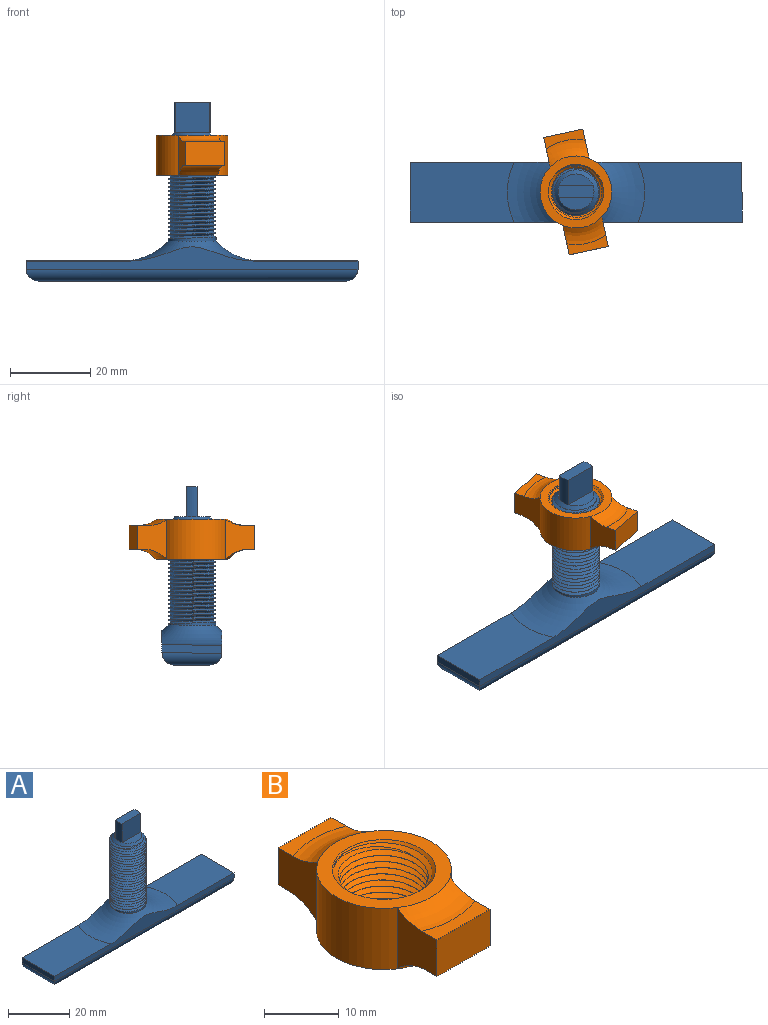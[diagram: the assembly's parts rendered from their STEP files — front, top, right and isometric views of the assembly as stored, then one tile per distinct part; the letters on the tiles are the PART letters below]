
ASSEMBLY  parts=2 mates=1
PART A: 24 faces, bbox 83x60.2x44.5 mm
  f0: plane 8.5x3.02mm, normal (0,0,1), area 18.7mm2, adj f15,f22
  f1: plane 26.04x15mm, normal (0,0,1), area 373.2mm2, adj f2,f4,f5,f12
  f2: plane 83x5.55mm, normal (0,-1,0), area 215.5mm2, adj f1,f3,f5,f6,f8,f12
  f3: plane 15x2mm, normal (1,0,0), area 30mm2, adj f2,f4,f6,f9
  f4: plane 83x5.55mm, normal (0,1,0), area 215.5mm2, adj f1,f3,f5,f6,f11,f12
  f5: plane 15x2mm, normal (-1,0,0), area 30mm2, adj f1,f2,f4,f10
  f6: plane 26.04x15mm, normal (0,0,1), area 373.2mm2, adj f2,f3,f4,f12
  f7: plane 77x9mm, normal (0,0,-1), area 693mm2, adj f8,f9,f10,f11
  f8: cylinder r=3mm len=83mm, axis (1,0,0), area 377mm2, adj f2,f7,f9,f10
  f9: cylinder r=3mm len=15mm, axis (0,1,0), area 56.5mm2, adj f3,f7,f8,f11
  f10: cylinder r=3mm len=15mm, axis (0,-1,0), area 56.5mm2, adj f5,f7,f8,f11
  f11: cylinder r=3mm len=83mm, axis (-1,0,0), area 377mm2, adj f4,f7,f9,f10
  f12: torus R=17.18mm, axis (0,0,1), area 440.4mm2, adj f1,f2,f4,f6,f13
  f13: cylinder r=6mm len=25.5mm, axis (0,0,1), area -242mm2, adj f12,f15,f16,f17,f18
  f14: plane 8.5x3.02mm, normal (0,0,1), area 18.7mm2, adj f15,f20
  f15: cone r=4.5mm half-angle=45deg, axis (0,0,-1), area 49.1mm2, adj f0,f13,f14,f17,f18,f19,f21
  f16: plane 0.98x0.84mm, normal (0,1,0), area 0.4mm2, adj f13,f17,f18
  f17: bspline ~26.49x13.86mm, area 882.5mm2, adj f13,f15,f16,f18
  f18: bspline ~26.49x13.86mm, area 863.6mm2, adj f13,f15,f16,f17
  f19: cylinder r=4.5mm len=7.5mm, axis (0,0,-1), area 22.6mm2, adj f15,f20,f22,f23
  f20: plane 8.5x7.5mm, normal (0,1,0), area 63.7mm2, adj f14,f19,f21,f23
  f21: cylinder r=4.5mm len=7.5mm, axis (0,0,-1), area 22.6mm2, adj f15,f20,f22,f23
  f22: plane 8.5x7.5mm, normal (0,-1,0), area 63.8mm2, adj f0,f19,f21,f23
  f23: plane 9x2.96mm, normal (0,0,1), area 26.1mm2, adj f19,f20,f21,f22
PART B: 25 faces, bbox 22.9x40.9x14.7 mm
  f0: cylinder r=5.9mm len=11.8mm, axis (0,0,-1), area 4.4mm2, adj f20,f21,f23,f24
  f1: cylinder r=9mm len=14.97mm, axis (0,0,-1), area 176.7mm2, adj f3,f4,f8,f11
  f2: cylinder r=9mm len=14.97mm, axis (0,0,-1), area 176.7mm2, adj f3,f4,f9,f10
  f3: plane 18x18mm, normal (0,0,1), area 104.9mm2, adj f1,f2,f16,f18,f21
  f4: plane 18x18mm, normal (0,0,-1), area 104.9mm2, adj f1,f2,f15,f17,f19
  f5: plane 10x6mm, normal (0,-1,0), area 60mm2, adj f6,f7,f8,f9
  f6: plane 10x2.83mm, normal (0,0,1), area 21.7mm2, adj f5,f8,f9,f18
  f7: plane 10x1.79mm, normal (0,0,-1), area 11.8mm2, adj f5,f8,f9,f17
  f8: plane 10.36x7.87mm, normal (-1,0,0), area 51.8mm2, adj f1,f5,f6,f7,f17,f18
  f9: plane 10.36x7.88mm, normal (1,0,0), area 51.8mm2, adj f2,f5,f6,f7,f17,f18
  f10: plane 10.36x7.87mm, normal (1,0,0), area 51.8mm2, adj f2,f12,f13,f14,f15,f16
  f11: plane 10.36x7.88mm, normal (-1,0,0), area 51.8mm2, adj f1,f12,f13,f14,f15,f16
  f12: plane 10x1.79mm, normal (0,0,-1), area 11.8mm2, adj f10,f11,f14,f15
  f13: plane 10x2.83mm, normal (0,0,1), area 21.7mm2, adj f10,f11,f14,f16
  f14: plane 10x6mm, normal (0,1,0), area 60mm2, adj f10,f11,f12,f13
  f15: torus R=14.12mm, axis (0,0,1), area 62.6mm2, adj f4,f10,f11,f12
  f16: torus R=13.15mm, axis (0,0,1), area 47.8mm2, adj f3,f10,f11,f13
  f17: torus R=14.12mm, axis (0,0,1), area 62.6mm2, adj f4,f7,f8,f9
  f18: torus R=13.15mm, axis (0,0,1), area 47.8mm2, adj f3,f6,f8,f9
  f19: cone r=5.9mm half-angle=45deg, axis (0,0,-1), area 39.7mm2, adj f4,f20,f22,f23
  f20: cone r=5.9mm half-angle=45deg, axis (0,0,-1), area 0mm2, adj f0,f19,f24
  f21: cone r=5.9mm half-angle=45deg, axis (0,0,1), area 34.2mm2, adj f0,f3,f23,f24
  f22: plane 0.79x0.58mm, normal (0,1,0), area 0.1mm2, adj f19,f23,f24
  f23: bspline ~15.58x13.49mm, area 343mm2, adj f0,f19,f21,f22,f24
  f24: bspline ~15.58x13.49mm, area 310.7mm2, adj f0,f20,f21,f22,f23
PLACE A rot(axis=(0.96,-0.15,0.23),0deg) t=(0.13,-1.92,-6.7)mm
PLACE B rot(axis=(0,0,1),12.2deg) t=(0.13,-1.92,19.7)mm
MATE cylindrical A.f12 <-> B.f1  axis (0,0,1) through (0.13,-1.92,30.3)mm
